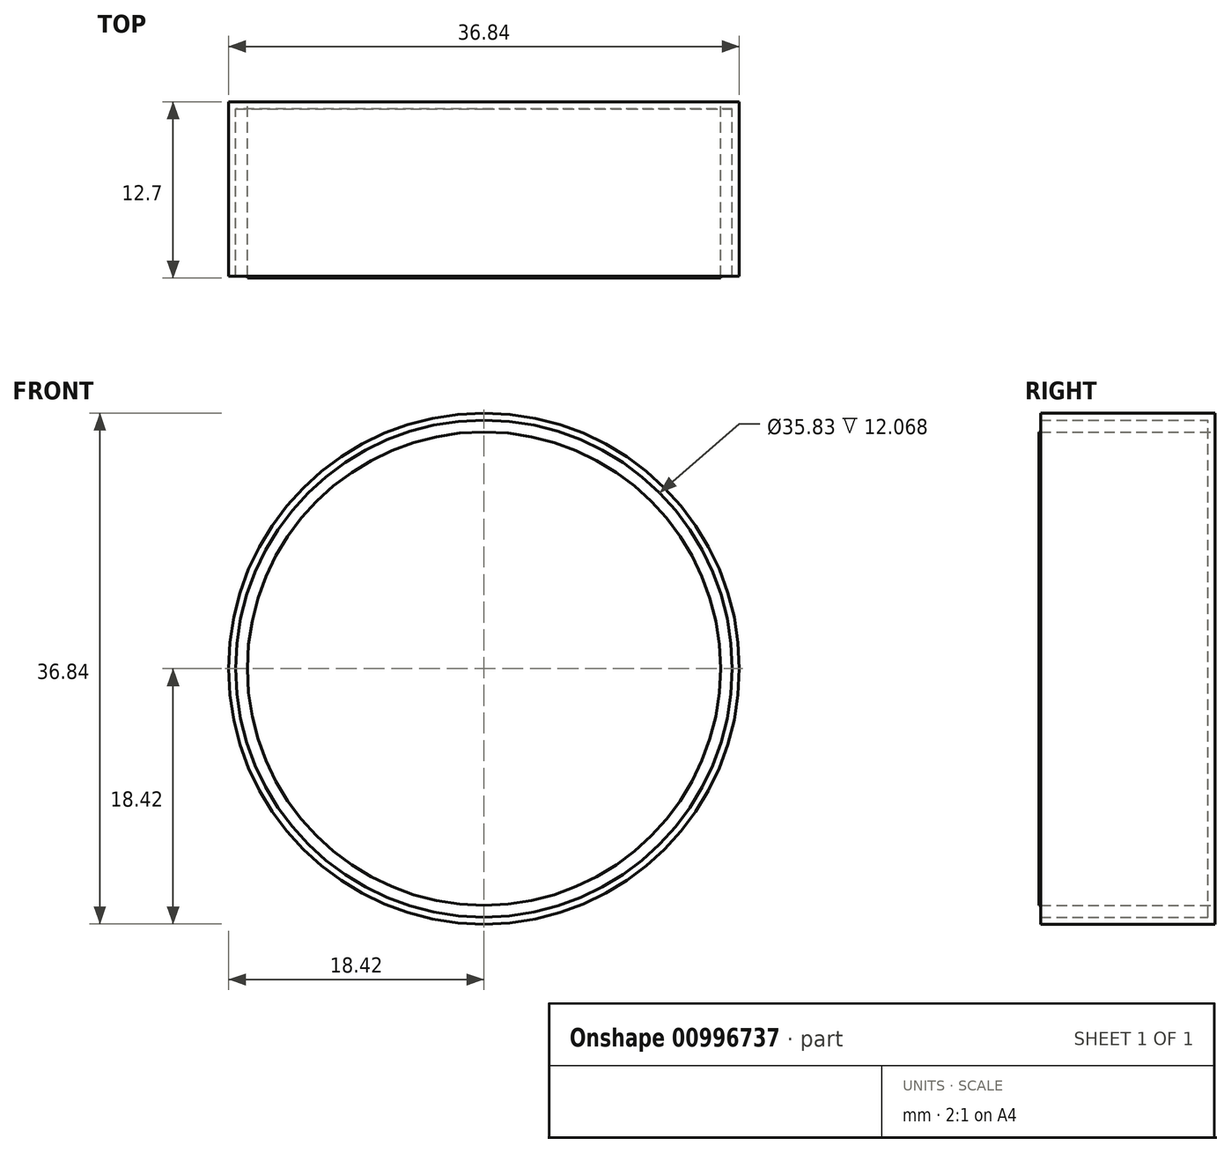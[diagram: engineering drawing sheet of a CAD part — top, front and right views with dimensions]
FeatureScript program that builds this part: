
annotation { "Feature Type Name" : "Feature", "Feature Type Description" : "" }
export const myFeature = defineFeature(function(context is Context, id is Id, definition is map)
    precondition{}
    {
        {
            var Q0;
            Q0=qCreatedBy(makeId("Front.planeOp"),FACE);
            var sketch = newSketch(context, id + "F0", { "sketchPlane" : qUnion([Q0])});
            skCircle(sketch, "E0", {"center": v(0, 0) * mm, "radius": 17.06 * mm});
            skSolve(sketch);
        }
        {
            var Q0;
            Q0=makeQuery(id+"F0.imprint","IMPRINT",FACE,{"disambiguationData":[TD([[makeQuery(id+"F0.imprint","IMPRINT",EDGE,{"derivedFrom":sQuery(id+"F0.wireOp",EDGE,"E0")}),1.0]])]});
            extrude(context, id + "F1", {"entities" : qUnion([Q0]), "depth" : 12.7 * mm, "offsetDistance" : 25.4 * mm});
        }
        {
            var Q0;
            Q0=qCreatedBy(makeId("Top.planeOp"),FACE);
            var sketch = newSketch(context, id + "F2", { "sketchPlane" : qUnion([Q0])});
            skLineSegment(sketch, "E1", {"start": v(0, 0) * mm, "end": v(0, 10.7) * mm});
            skSolve(sketch);
        }
        {
            var Q0;
            Q0=qCreatedBy(makeId("Top.planeOp"),FACE);
            var sketch = newSketch(context, id + "F3", { "sketchPlane" : qUnion([Q0])});
            skFitSpline(sketch, "E2", {"points": [v(-16.59, 0) * mm, v(-14.48, 1.56) * mm, v(-9.78, 3.26) * mm, v(0, 3.82) * mm], "startDerivative": vector(4.55, 12.87) * mm, "endDerivative": vector(21.3, 0.63) * mm});
            skSolve(sketch);
        }
        {
            var Q0;
            Q0=sQuery(id+"F3.wireOp",EDGE,"E2");
            var Q1;
            Q1=sQuery(id+"F2.wireOp",EDGE,"E1");
            revolve(context, id + "F4", {"bodyType" : ToolBodyType.SURFACE, "surfaceOperationType" : NewSurfaceOperationType.NEW, "surfaceEntities" : qUnion([Q0]), "axis" : qUnion([Q1]), "revolveType" : RevolveType.FULL});
        }
        {
            var Q0;
            Q0=qCreatedBy(makeId("Front.planeOp"),FACE);
            var sketch = newSketch(context, id + "F5", { "sketchPlane" : qUnion([Q0])});
            skCircle(sketch, "E3", {"center": v(0, 0) * mm, "radius": 18.42 * mm});
            skSolve(sketch);
        }
        {
            var Q0;
            Q0=makeQuery(id+"F5.imprint","IMPRINT",FACE,{"disambiguationData":[TD([[makeQuery(id+"F5.imprint","IMPRINT",EDGE,{"derivedFrom":sQuery(id+"F5.wireOp",EDGE,"E3")}),1.0]])]});
            extrude(context, id + "F6", {"entities" : qUnion([Q0]), "depth" : 12.58 * mm, "offsetDistance" : 25.4 * mm});
        }
        {
            var Q0;
            Q0=makeQuery(id+"F6.opExtrude","CAP_FACE",FACE,{"disambiguationData":[OSD([sQuery(id+"F5.wireOp",EDGE,"E3")])],"isStart":false});
            shell(context, id + "F7", {"entities" : qUnion([Q0]), "thickness" : 0.5 * mm});
        }
    });
